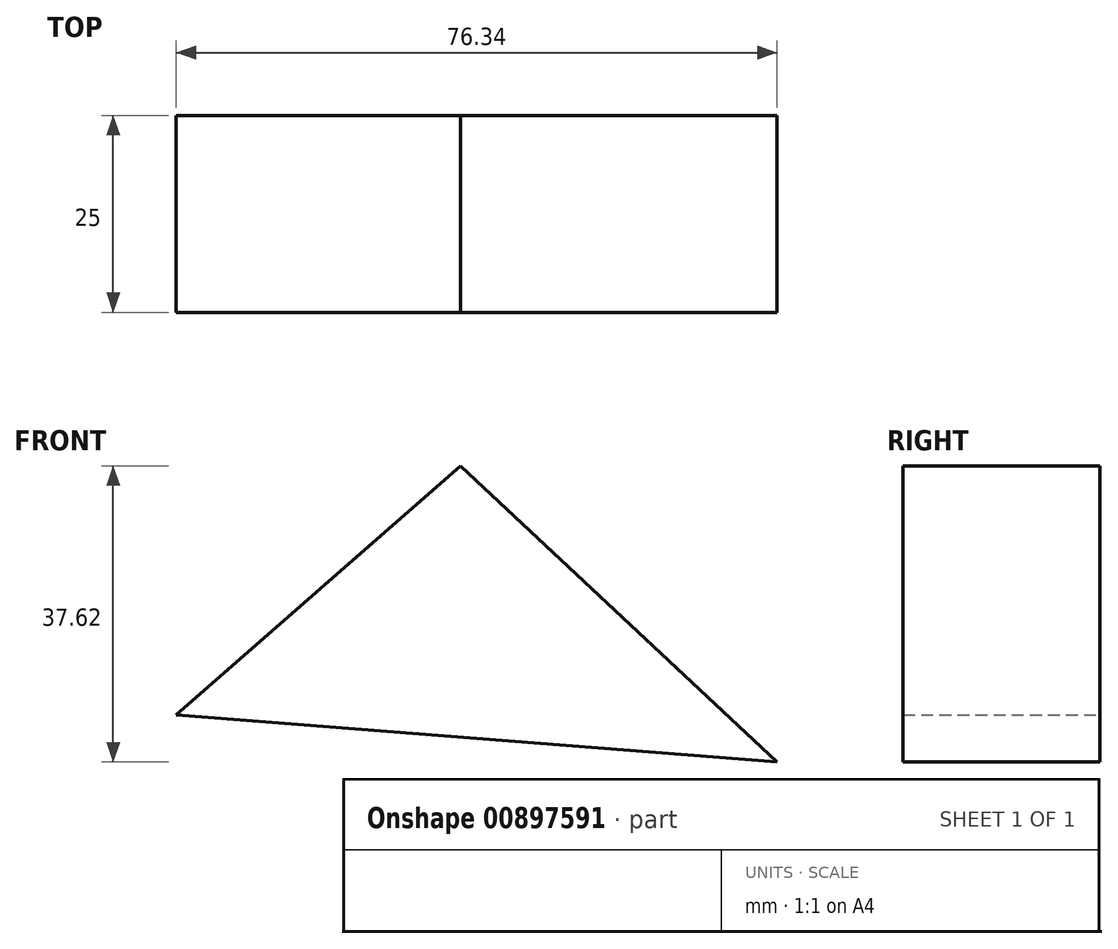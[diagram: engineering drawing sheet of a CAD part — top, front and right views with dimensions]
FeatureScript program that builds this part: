
annotation { "Feature Type Name" : "Feature", "Feature Type Description" : "" }
export const myFeature = defineFeature(function(context is Context, id is Id, definition is map)
    precondition{}
    {
        {
            var Q0;
            Q0=qCreatedBy(makeId("Front.planeOp"),FACE);
            var sketch = newSketch(context, id + "F0", { "sketchPlane" : qUnion([Q0])});
            skLineSegment(sketch, "E0", {"start": v(-39.66, -20.99) * mm, "end": v(45.33, 53.56) * mm});
            skLineSegment(sketch, "E1", {"start": v(-41.15, 45.8) * mm, "end": v(36.68, -26.95) * mm});
            skLineSegment(sketch, "E2", {"start": v(-39.66, -20.99) * mm, "end": v(36.68, -26.95) * mm});
            skSolve(sketch);
        }
        {
            var Q0;
            {var subQ0=sQuery(id+"F0.wireOp",EDGE,"E2");Q0=makeQuery(id+"F0.imprint","IMPRINT",FACE,{"disambiguationData":[TD([[makeQuery(id+"F0.imprint","IMPRINT",EDGE,{"derivedFrom":subQ0}),1.0]])]});}
            extrude(context, id + "F1", {"entities" : qUnion([Q0]), "depth" : 25 * mm, "offsetDistance" : 25 * mm});
        }
    });
